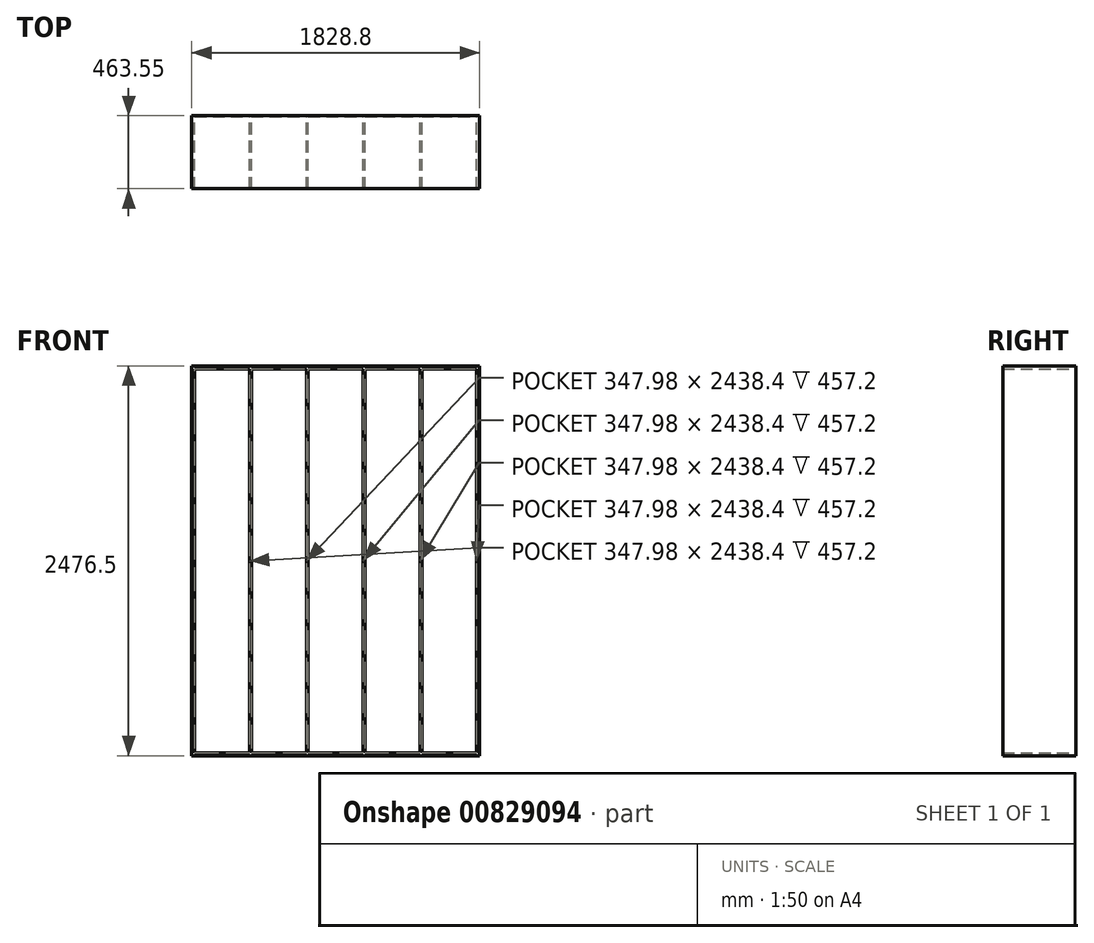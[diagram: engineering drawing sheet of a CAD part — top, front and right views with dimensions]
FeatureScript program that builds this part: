
annotation { "Feature Type Name" : "Feature", "Feature Type Description" : "" }
export const myFeature = defineFeature(function(context is Context, id is Id, definition is map)
    precondition{}
    {
        {
            var Q0;
            Q0=qCreatedBy(makeId("Front.planeOp"),FACE);
            var sketch = newSketch(context, id + "F0", { "sketchPlane" : qUnion([Q0])});
            skLineSegment(sketch, "E0.bottom", {"start": v(-1330.71, -1217.51) * mm, "end": v(459.99, -1217.51) * mm});
            skLineSegment(sketch, "E0.top", {"start": v(-1330.71, 1220.89) * mm, "end": v(459.99, 1220.89) * mm});
            skLineSegment(sketch, "E0.left", {"start": v(-1330.71, -1217.51) * mm, "end": v(-1330.71, 1220.89) * mm});
            skLineSegment(sketch, "E0.right", {"start": v(459.99, -1217.51) * mm, "end": v(459.99, 1220.89) * mm});
            skLineSegment(sketch, "E1.bottom", {"start": v(-982.73, 1220.89) * mm, "end": v(-970.03, 1220.89) * mm});
            skLineSegment(sketch, "E1.top", {"start": v(-982.73, -1217.51) * mm, "end": v(-970.03, -1217.51) * mm});
            skLineSegment(sketch, "E1.left", {"start": v(-982.73, 1220.89) * mm, "end": v(-982.73, -1217.51) * mm});
            skLineSegment(sketch, "E1.right", {"start": v(-970.03, 1220.89) * mm, "end": v(-970.03, -1217.51) * mm});
            skLineSegment(sketch, "E2.bottom", {"start": v(-622.05, 1220.89) * mm, "end": v(-609.35, 1220.89) * mm});
            skLineSegment(sketch, "E2.top", {"start": v(-622.05, -1217.51) * mm, "end": v(-609.35, -1217.51) * mm});
            skLineSegment(sketch, "E2.left", {"start": v(-622.05, 1220.89) * mm, "end": v(-622.05, -1217.51) * mm});
            skLineSegment(sketch, "E2.right", {"start": v(-609.35, 1220.89) * mm, "end": v(-609.35, -1217.51) * mm});
            skLineSegment(sketch, "E3.bottom", {"start": v(-261.37, 1220.89) * mm, "end": v(-248.67, 1220.89) * mm});
            skLineSegment(sketch, "E3.top", {"start": v(-261.37, -1217.51) * mm, "end": v(-248.67, -1217.51) * mm});
            skLineSegment(sketch, "E3.left", {"start": v(-261.37, 1220.89) * mm, "end": v(-261.37, -1217.51) * mm});
            skLineSegment(sketch, "E3.right", {"start": v(-248.67, 1220.89) * mm, "end": v(-248.67, -1217.51) * mm});
            skLineSegment(sketch, "E4.bottom", {"start": v(99.3, -1217.51) * mm, "end": v(112, -1217.51) * mm});
            skLineSegment(sketch, "E4.top", {"start": v(99.3, 1220.89) * mm, "end": v(112, 1220.89) * mm});
            skLineSegment(sketch, "E4.left", {"start": v(99.3, -1217.51) * mm, "end": v(99.3, 1220.89) * mm});
            skLineSegment(sketch, "E4.right", {"start": v(112, -1217.51) * mm, "end": v(112, 1220.89) * mm});
            skLineSegment(sketch, "E5", {"start": v(-1330.71, 1220.89) * mm, "end": v(-1349.76, 1220.89) * mm});
            skLineSegment(sketch, "E6", {"start": v(-1349.76, 1220.89) * mm, "end": v(-1349.76, -1217.51) * mm});
            skLineSegment(sketch, "E7", {"start": v(-1349.76, -1217.51) * mm, "end": v(-1330.71, -1217.51) * mm});
            skLineSegment(sketch, "E8", {"start": v(459.99, -1217.51) * mm, "end": v(479.04, -1217.51) * mm});
            skLineSegment(sketch, "E9", {"start": v(479.04, -1217.51) * mm, "end": v(479.04, 1220.89) * mm});
            skLineSegment(sketch, "E10", {"start": v(479.04, 1220.89) * mm, "end": v(459.99, 1220.89) * mm});
            skLineSegment(sketch, "E11", {"start": v(-1349.76, 1220.89) * mm, "end": v(-1349.76, 1239.94) * mm});
            skLineSegment(sketch, "E12", {"start": v(-1349.76, 1239.94) * mm, "end": v(479.04, 1239.94) * mm});
            skLineSegment(sketch, "E13", {"start": v(479.04, 1239.94) * mm, "end": v(479.04, 1220.89) * mm});
            skLineSegment(sketch, "E14", {"start": v(479.04, -1217.51) * mm, "end": v(479.04, -1236.56) * mm});
            skLineSegment(sketch, "E15", {"start": v(479.04, -1236.56) * mm, "end": v(-1349.76, -1236.56) * mm});
            skLineSegment(sketch, "E16", {"start": v(-1349.76, -1236.56) * mm, "end": v(-1349.76, -1217.51) * mm});
            skLineSegment(sketch, "E17", {"start": v(-1330.71, 89.26) * mm, "end": v(-982.73, 89.26) * mm, "construction": true});
            skLineSegment(sketch, "E18", {"start": v(-970.03, 92.02) * mm, "end": v(-622.05, 92.02) * mm, "construction": true});
            skLineSegment(sketch, "E19", {"start": v(-609.35, 90.52) * mm, "end": v(-261.37, 90.52) * mm, "construction": true});
            skLineSegment(sketch, "E20", {"start": v(-248.67, 93.36) * mm, "end": v(99.3, 93.36) * mm, "construction": true});
            skLineSegment(sketch, "E21", {"start": v(112, 96.19) * mm, "end": v(459.99, 96.19) * mm, "construction": true});
            skSolve(sketch);
        }
        {
            var Q0;
            {var subQ0=sQuery(id+"F0.wireOp",EDGE,"E5");var subQ1=makeQuery(id+"F0.imprint","IMPRINT",EDGE,{"derivedFrom":subQ0});var subQ19=sQuery(id+"F0.wireOp",EDGE,"E0.left");var subQ21=sQuery(id+"F0.wireOp",EDGE,"E0.right");var subQ23=sQuery(id+"F0.wireOp",EDGE,"E7");var subQ24=makeQuery(id+"F0.imprint","IMPRINT",EDGE,{"derivedFrom":subQ23});Q0=qUnion([makeQuery(id+"F0.imprint","IMPRINT",FACE,{"disambiguationData":[TD([[makeQuery(id+"F0.imprint","IMPRINT",EDGE,{"derivedFrom":subQ19}),1.0]])]}),makeQuery(id+"F0.imprint","IMPRINT",FACE,{"disambiguationData":[TD([[makeQuery(id+"F0.imprint","IMPRINT",EDGE,{"derivedFrom":subQ21}),-1.0]])]}),makeQuery(id+"F0.imprint","IMPRINT",FACE,{"disambiguationData":[TD([[subQ24,-1.0]])]}),makeQuery(id+"F0.imprint","IMPRINT",FACE,{"disambiguationData":[TD([[subQ1,-1.0]])]})]);}
            var Q1;
            {var subQ0=sQuery(id+"F0.wireOp",EDGE,"E1.left");Q1=makeQuery(id+"F0.imprint","IMPRINT",FACE,{"disambiguationData":[TD([[makeQuery(id+"F0.imprint","IMPRINT",EDGE,{"derivedFrom":subQ0}),1.0]])]});}
            var Q2;
            {var subQ0=sQuery(id+"F0.wireOp",EDGE,"E2.left");Q2=makeQuery(id+"F0.imprint","IMPRINT",FACE,{"disambiguationData":[TD([[makeQuery(id+"F0.imprint","IMPRINT",EDGE,{"derivedFrom":subQ0}),1.0]])]});}
            var Q3;
            {var subQ2=sQuery(id+"F0.wireOp",EDGE,"E3.left");Q3=makeQuery(id+"F0.imprint","IMPRINT",FACE,{"disambiguationData":[TD([[makeQuery(id+"F0.imprint","IMPRINT",EDGE,{"derivedFrom":subQ2}),1.0]])]});}
            var Q4;
            {var subQ0=sQuery(id+"F0.wireOp",EDGE,"E4.left");Q4=makeQuery(id+"F0.imprint","IMPRINT",FACE,{"disambiguationData":[TD([[makeQuery(id+"F0.imprint","IMPRINT",EDGE,{"derivedFrom":subQ0}),-1.0]])]});}
            extrude(context, id + "F1", {"entities" : qUnion([Q0, Q1, Q2, Q3, Q4]), "depth" : 457.2 * mm, "offsetDistance" : 25.4 * mm});
        }
        {
            var Q0;
            Q0=makeQuery(id+"F1.opExtrude","CAP_FACE",FACE,{"disambiguationData":[OSD([sQuery(id+"F0.wireOp",EDGE,"E0.bottom"),sQuery(id+"F0.wireOp",EDGE,"E0.top"),sQuery(id+"F0.wireOp",EDGE,"E0.left"),sQuery(id+"F0.wireOp",EDGE,"E0.right"),sQuery(id+"F0.wireOp",EDGE,"E1.left"),sQuery(id+"F0.wireOp",EDGE,"E1.right"),sQuery(id+"F0.wireOp",EDGE,"E2.left"),sQuery(id+"F0.wireOp",EDGE,"E2.right"),sQuery(id+"F0.wireOp",EDGE,"E3.left"),sQuery(id+"F0.wireOp",EDGE,"E3.right"),sQuery(id+"F0.wireOp",EDGE,"E4.left"),sQuery(id+"F0.wireOp",EDGE,"E4.right"),sQuery(id+"F0.wireOp",EDGE,"E6"),sQuery(id+"F0.wireOp",EDGE,"E9"),sQuery(id+"F0.wireOp",EDGE,"E11"),sQuery(id+"F0.wireOp",EDGE,"E12"),sQuery(id+"F0.wireOp",EDGE,"E13"),sQuery(id+"F0.wireOp",EDGE,"E14"),sQuery(id+"F0.wireOp",EDGE,"E15"),sQuery(id+"F0.wireOp",EDGE,"E16")])],"isStart":true});
            var sketch = newSketch(context, id + "F2", { "sketchPlane" : qUnion([Q0])});
            skLineSegment(sketch, "E22.0", {"start": v(1349.76, 1239.94) * mm, "end": v(-479.04, 1239.94) * mm});
            skLineSegment(sketch, "E22.1", {"start": v(-479.04, -1236.56) * mm, "end": v(-479.04, 1239.94) * mm});
            skLineSegment(sketch, "E22.2", {"start": v(1349.76, 1239.94) * mm, "end": v(1349.76, -1236.56) * mm});
            skLineSegment(sketch, "E22.3", {"start": v(-479.04, -1236.56) * mm, "end": v(1349.76, -1236.56) * mm});
            skSolve(sketch);
        }
        {
            var Q0;
            Q0 = qSketchRegion(id + "F2", true);
            extrude(context, id + "F3", {"entities" : qUnion([Q0]), "operationType" : NewBodyOperationType.ADD, "depth" : 6.35 * mm, "offsetDistance" : 25.4 * mm});
        }
    });
